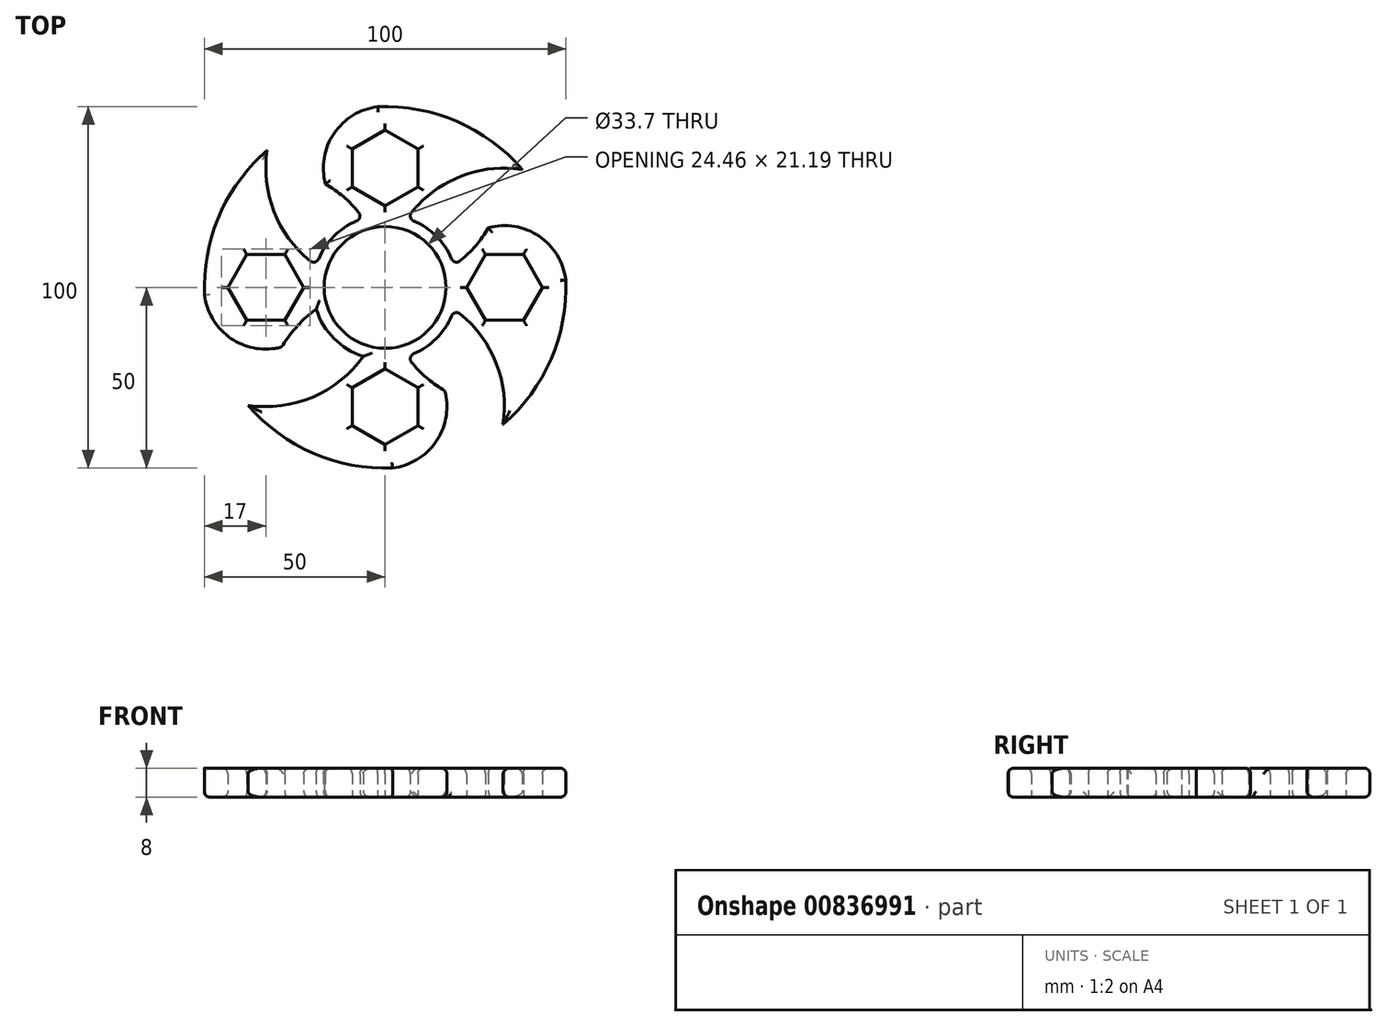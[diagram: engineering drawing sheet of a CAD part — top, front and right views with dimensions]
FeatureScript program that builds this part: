
annotation { "Feature Type Name" : "Feature", "Feature Type Description" : "" }
export const myFeature = defineFeature(function(context is Context, id is Id, definition is map)
    precondition{}
    {
        {
            var Q0;
            Q0=qCreatedBy(makeId("Top.planeOp"),FACE);
            var sketch = newSketch(context, id + "F0", { "sketchPlane" : qUnion([Q0])});
            skCircle(sketch, "E0", {"center": v(0, 0) * mm, "radius": 16.85 * mm});
            skArc(sketch, "E1", {"start": v(-19.06, -6.06) * mm, "mid": v(-14.14, -14.14) * mm, "end": v(-6.06, -19.06) * mm});
            skLineSegment(sketch, "E2.0", {"start": v(-22.5, 0) * mm, "end": v(-27.75, -9.1) * mm});
            skLineSegment(sketch, "E2.1", {"start": v(-27.75, -9.1) * mm, "end": v(-38.25, -9.1) * mm});
            skLineSegment(sketch, "E2.2", {"start": v(-38.25, -9.1) * mm, "end": v(-43.5, 0) * mm});
            skLineSegment(sketch, "E2.3", {"start": v(-43.5, 0) * mm, "end": v(-38.25, 9.1) * mm});
            skLineSegment(sketch, "E2.4", {"start": v(-38.25, 9.1) * mm, "end": v(-27.75, 9.1) * mm});
            skLineSegment(sketch, "E2.5", {"start": v(-27.75, 9.1) * mm, "end": v(-22.5, 0) * mm});
            skLineSegment(sketch, "E3.0", {"start": v(0, 22.5) * mm, "end": v(-9.1, 27.75) * mm});
            skLineSegment(sketch, "E3.1", {"start": v(-9.1, 27.75) * mm, "end": v(-9.1, 38.25) * mm});
            skLineSegment(sketch, "E3.2", {"start": v(-9.1, 38.25) * mm, "end": v(0, 43.5) * mm});
            skLineSegment(sketch, "E3.3", {"start": v(0, 43.5) * mm, "end": v(9.1, 38.25) * mm});
            skLineSegment(sketch, "E3.4", {"start": v(9.1, 38.25) * mm, "end": v(9.1, 27.75) * mm});
            skLineSegment(sketch, "E3.5", {"start": v(9.1, 27.75) * mm, "end": v(0, 22.5) * mm});
            skLineSegment(sketch, "E4.0", {"start": v(22.5, 0) * mm, "end": v(27.75, 9.1) * mm});
            skLineSegment(sketch, "E4.1", {"start": v(27.75, 9.1) * mm, "end": v(38.25, 9.1) * mm});
            skLineSegment(sketch, "E4.2", {"start": v(38.25, 9.1) * mm, "end": v(43.5, 0) * mm});
            skLineSegment(sketch, "E4.3", {"start": v(43.5, 0) * mm, "end": v(38.25, -9.1) * mm});
            skLineSegment(sketch, "E4.4", {"start": v(38.25, -9.1) * mm, "end": v(27.75, -9.1) * mm});
            skLineSegment(sketch, "E4.5", {"start": v(27.75, -9.1) * mm, "end": v(22.5, 0) * mm});
            skLineSegment(sketch, "E5.0", {"start": v(0, -22.5) * mm, "end": v(9.1, -27.75) * mm});
            skLineSegment(sketch, "E5.1", {"start": v(9.1, -27.75) * mm, "end": v(9.1, -38.25) * mm});
            skLineSegment(sketch, "E5.2", {"start": v(9.1, -38.25) * mm, "end": v(0, -43.5) * mm});
            skLineSegment(sketch, "E5.3", {"start": v(0, -43.5) * mm, "end": v(-9.1, -38.25) * mm});
            skLineSegment(sketch, "E5.4", {"start": v(-9.1, -38.25) * mm, "end": v(-9.1, -27.75) * mm});
            skLineSegment(sketch, "E5.5", {"start": v(-9.1, -27.75) * mm, "end": v(0, -22.5) * mm});
            skArc(sketch, "E6", {"start": v(32.64, -37.88) * mm, "mid": v(30.35, -20.05) * mm, "end": v(19.06, -6.06) * mm});
            skArc(sketch, "E7", {"start": v(37.88, 32.64) * mm, "mid": v(20.05, 30.35) * mm, "end": v(6.06, 19.06) * mm});
            skArc(sketch, "E8", {"start": v(-32.64, 37.88) * mm, "mid": v(-45.87, 19.9) * mm, "end": v(-49.96, -2.06) * mm});
            skPoint(sketch, "E9", {"position": v(-28.58, -16.5) * mm});
            skArc(sketch, "E10.trimOffspring", {"start": v(-49.96, -2.06) * mm, "mid": v(-42.56, -14.15) * mm, "end": v(-28.58, -16.5) * mm});
            skArc(sketch, "E11.trimOffspring", {"start": v(-37.88, -32.64) * mm, "mid": v(-20.05, -30.35) * mm, "end": v(-6.06, -19.06) * mm});
            skArc(sketch, "E12.trimOffspring", {"start": v(0, -0.7) * mm, "mid": v(0, -0.7) * mm, "end": v(0, -0.7) * mm});
            skArc(sketch, "E13.trimOffspring", {"start": v(-32.64, 37.88) * mm, "mid": v(-30.35, 20.05) * mm, "end": v(-19.06, 6.06) * mm});
            skArc(sketch, "E14.trimOffspring", {"start": v(-6.06, 19.06) * mm, "mid": v(-10.76, 24.38) * mm, "end": v(-16.5, 28.58) * mm});
            skArc(sketch, "E15.trimOffspring", {"start": v(-6.06, 19.06) * mm, "mid": v(-14.14, 14.14) * mm, "end": v(-19.06, 6.06) * mm});
            skArc(sketch, "E16.trimOffspring", {"start": v(-2.06, 49.96) * mm, "mid": v(-14.15, 42.56) * mm, "end": v(-16.5, 28.58) * mm});
            skArc(sketch, "E17.trimOffspring", {"start": v(37.88, 32.64) * mm, "mid": v(19.9, 45.87) * mm, "end": v(-2.06, 49.96) * mm});
            skArc(sketch, "E18.trimOffspring", {"start": v(49.96, 2.06) * mm, "mid": v(42.56, 14.15) * mm, "end": v(28.58, 16.5) * mm});
            skArc(sketch, "E19.trimOffspring", {"start": v(-37.88, -32.64) * mm, "mid": v(-19.9, -45.87) * mm, "end": v(2.06, -49.96) * mm});
            skArc(sketch, "E20.trimOffspring", {"start": v(32.64, -37.88) * mm, "mid": v(45.87, -19.9) * mm, "end": v(49.96, 2.06) * mm});
            skArc(sketch, "E21.trimOffspring", {"start": v(2.06, -49.96) * mm, "mid": v(14.15, -42.56) * mm, "end": v(16.5, -28.58) * mm});
            skArc(sketch, "E22.trimOffspring", {"start": v(-19.06, -6.06) * mm, "mid": v(-24.38, -10.76) * mm, "end": v(-28.58, -16.5) * mm});
            skArc(sketch, "E23.trimOffspring", {"start": v(0, 0.7) * mm, "mid": v(0, 0.7) * mm, "end": v(0, 0.7) * mm});
            skArc(sketch, "E24.trimOffspring", {"start": v(6.06, -19.06) * mm, "mid": v(10.76, -24.38) * mm, "end": v(16.5, -28.58) * mm});
            skArc(sketch, "E25.trimOffspring", {"start": v(6.06, -19.06) * mm, "mid": v(14.14, -14.14) * mm, "end": v(19.06, -6.06) * mm});
            skArc(sketch, "E26.trimOffspring", {"start": v(19.06, 6.06) * mm, "mid": v(14.14, 14.14) * mm, "end": v(6.06, 19.06) * mm});
            skArc(sketch, "E27.trimOffspring", {"start": v(19.06, 6.06) * mm, "mid": v(24.38, 10.76) * mm, "end": v(28.58, 16.5) * mm});
            skSolve(sketch);
        }
        {
            var Q0;
            Q0 = qSketchRegion(id + "F0", true);
            extrude(context, id + "F1", {"entities" : qUnion([Q0]), "depth" : 8 * mm, "offsetDistance" : 25 * mm});
        }
        {
            var Q0;
            Q0=makeQuery(id+"F1.opExtrude","CAP_EDGE",EDGE,{"disambiguationData":[OSD([sQuery(id+"F0.wireOp",EDGE,"E5.3")])],"isStart":false});
            var Q1;
            Q1=makeQuery(id+"F1.opExtrude","CAP_EDGE",EDGE,{"disambiguationData":[OSD([sQuery(id+"F0.wireOp",EDGE,"E5.2")])],"isStart":false});
            var Q2;
            Q2=makeQuery(id+"F1.opExtrude","CAP_EDGE",EDGE,{"disambiguationData":[OSD([sQuery(id+"F0.wireOp",EDGE,"E5.4")])],"isStart":false});
            var Q3;
            Q3=makeQuery(id+"F1.opExtrude","CAP_EDGE",EDGE,{"disambiguationData":[OSD([sQuery(id+"F0.wireOp",EDGE,"E5.5")])],"isStart":false});
            var Q4;
            Q4=makeQuery(id+"F1.opExtrude","CAP_EDGE",EDGE,{"disambiguationData":[OSD([sQuery(id+"F0.wireOp",EDGE,"E5.0")])],"isStart":false});
            var Q5;
            Q5=makeQuery(id+"F1.opExtrude","CAP_EDGE",EDGE,{"disambiguationData":[OSD([sQuery(id+"F0.wireOp",EDGE,"E5.1")])],"isStart":false});
            var Q6;
            Q6=makeQuery(id+"F1.opExtrude","CAP_EDGE",EDGE,{"disambiguationData":[OSD([sQuery(id+"F0.wireOp",EDGE,"E24.trimOffspring")])],"isStart":false});
            var Q7;
            Q7=makeQuery(id+"F1.opExtrude","CAP_EDGE",EDGE,{"disambiguationData":[OSD([sQuery(id+"F0.wireOp",EDGE,"E21.trimOffspring")])],"isStart":false});
            var Q8;
            Q8=makeQuery(id+"F1.opExtrude","SWEPT_EDGE",EDGE,{"disambiguationData":[OSD([sQuery(id+"F0.wireOp",EDGE,"E21.trimOffspring"),sQuery(id+"F0.wireOp",EDGE,"E24.trimOffspring")])]});
            var Q9;
            Q9=makeQuery(id+"F1.opExtrude","CAP_EDGE",EDGE,{"disambiguationData":[OSD([sQuery(id+"F0.wireOp",EDGE,"E11.trimOffspring")])],"isStart":false});
            var Q10;
            Q10=makeQuery(id+"F1.opExtrude","CAP_EDGE",EDGE,{"disambiguationData":[OSD([sQuery(id+"F0.wireOp",EDGE,"E25.trimOffspring")])],"isStart":false});
            var Q11;
            Q11=makeQuery(id+"F1.opExtrude","SWEPT_EDGE",EDGE,{"disambiguationData":[OSD([sQuery(id+"F0.wireOp",EDGE,"E24.trimOffspring"),sQuery(id+"F0.wireOp",EDGE,"E25.trimOffspring")])]});
            var Q12;
            Q12=makeQuery(id+"F1.opExtrude","CAP_EDGE",EDGE,{"disambiguationData":[OSD([sQuery(id+"F0.wireOp",EDGE,"E6")])],"isStart":false});
            var Q13;
            Q13=makeQuery(id+"F1.opExtrude","CAP_EDGE",EDGE,{"disambiguationData":[OSD([sQuery(id+"F0.wireOp",EDGE,"E27.trimOffspring")])],"isStart":false});
            var Q14;
            Q14=makeQuery(id+"F1.opExtrude","SWEPT_EDGE",EDGE,{"disambiguationData":[OSD([sQuery(id+"F0.wireOp",EDGE,"E7"),sQuery(id+"F0.wireOp",EDGE,"E26.trimOffspring")])]});
            var Q15;
            Q15=makeQuery(id+"F1.opExtrude","CAP_EDGE",EDGE,{"disambiguationData":[OSD([sQuery(id+"F0.wireOp",EDGE,"E26.trimOffspring")])],"isStart":false});
            var Q16;
            Q16=makeQuery(id+"F1.opExtrude","CAP_EDGE",EDGE,{"disambiguationData":[OSD([sQuery(id+"F0.wireOp",EDGE,"E17.trimOffspring")])],"isStart":false});
            var Q17;
            Q17=makeQuery(id+"F1.opExtrude","CAP_EDGE",EDGE,{"disambiguationData":[OSD([sQuery(id+"F0.wireOp",EDGE,"E14.trimOffspring")])],"isStart":false});
            var Q18;
            Q18=makeQuery(id+"F1.opExtrude","CAP_EDGE",EDGE,{"disambiguationData":[OSD([sQuery(id+"F0.wireOp",EDGE,"E16.trimOffspring")])],"isStart":false});
            var Q19;
            Q19=makeQuery(id+"F1.opExtrude","CAP_EDGE",EDGE,{"disambiguationData":[OSD([sQuery(id+"F0.wireOp",EDGE,"E13.trimOffspring")])],"isStart":false});
            var Q20;
            Q20=makeQuery(id+"F1.opExtrude","CAP_EDGE",EDGE,{"disambiguationData":[OSD([sQuery(id+"F0.wireOp",EDGE,"E13.trimOffspring")])],"isStart":true});
            var Q21;
            Q21=makeQuery(id+"F1.opExtrude","SWEPT_EDGE",EDGE,{"disambiguationData":[OSD([sQuery(id+"F0.wireOp",EDGE,"E10.trimOffspring"),sQuery(id+"F0.wireOp",EDGE,"E22.trimOffspring")])]});
            var Q22;
            Q22=makeQuery(id+"F1.opExtrude","CAP_EDGE",EDGE,{"disambiguationData":[OSD([sQuery(id+"F0.wireOp",EDGE,"E22.trimOffspring")])],"isStart":true});
            var Q23;
            Q23=makeQuery(id+"F1.opExtrude","CAP_EDGE",EDGE,{"disambiguationData":[OSD([sQuery(id+"F0.wireOp",EDGE,"E22.trimOffspring")])],"isStart":false});
            var Q24;
            Q24=makeQuery(id+"F1.opExtrude","CAP_EDGE",EDGE,{"disambiguationData":[OSD([sQuery(id+"F0.wireOp",EDGE,"E15.trimOffspring")])],"isStart":false});
            var Q25;
            Q25=makeQuery(id+"F1.opExtrude","CAP_EDGE",EDGE,{"disambiguationData":[OSD([sQuery(id+"F0.wireOp",EDGE,"E1")])],"isStart":false});
            var Q26;
            Q26=makeQuery(id+"F1.opExtrude","CAP_EDGE",EDGE,{"disambiguationData":[OSD([sQuery(id+"F0.wireOp",EDGE,"E2.0")])],"isStart":false});
            var Q27;
            Q27=makeQuery(id+"F1.opExtrude","CAP_EDGE",EDGE,{"disambiguationData":[OSD([sQuery(id+"F0.wireOp",EDGE,"E2.1")])],"isStart":false});
            var Q28;
            Q28=makeQuery(id+"F1.opExtrude","CAP_EDGE",EDGE,{"disambiguationData":[OSD([sQuery(id+"F0.wireOp",EDGE,"E2.2")])],"isStart":false});
            var Q29;
            Q29=makeQuery(id+"F1.opExtrude","CAP_EDGE",EDGE,{"disambiguationData":[OSD([sQuery(id+"F0.wireOp",EDGE,"E2.3")])],"isStart":false});
            var Q30;
            Q30=makeQuery(id+"F1.opExtrude","CAP_EDGE",EDGE,{"disambiguationData":[OSD([sQuery(id+"F0.wireOp",EDGE,"E2.4")])],"isStart":false});
            var Q31;
            Q31=makeQuery(id+"F1.opExtrude","CAP_EDGE",EDGE,{"disambiguationData":[OSD([sQuery(id+"F0.wireOp",EDGE,"E2.5")])],"isStart":false});
            var Q32;
            Q32=makeQuery(id+"F1.opExtrude","CAP_EDGE",EDGE,{"disambiguationData":[OSD([sQuery(id+"F0.wireOp",EDGE,"E20.trimOffspring")])],"isStart":false});
            var Q33;
            Q33=makeQuery(id+"F1.opExtrude","CAP_EDGE",EDGE,{"disambiguationData":[OSD([sQuery(id+"F0.wireOp",EDGE,"E18.trimOffspring")])],"isStart":false});
            var Q34;
            Q34=makeQuery(id+"F1.opExtrude","CAP_EDGE",EDGE,{"disambiguationData":[OSD([sQuery(id+"F0.wireOp",EDGE,"E4.4")])],"isStart":false});
            var Q35;
            Q35=makeQuery(id+"F1.opExtrude","CAP_EDGE",EDGE,{"disambiguationData":[OSD([sQuery(id+"F0.wireOp",EDGE,"E4.5")])],"isStart":false});
            var Q36;
            Q36=makeQuery(id+"F1.opExtrude","CAP_EDGE",EDGE,{"disambiguationData":[OSD([sQuery(id+"F0.wireOp",EDGE,"E4.0")])],"isStart":false});
            var Q37;
            Q37=makeQuery(id+"F1.opExtrude","CAP_EDGE",EDGE,{"disambiguationData":[OSD([sQuery(id+"F0.wireOp",EDGE,"E4.1")])],"isStart":false});
            var Q38;
            Q38=makeQuery(id+"F1.opExtrude","CAP_EDGE",EDGE,{"disambiguationData":[OSD([sQuery(id+"F0.wireOp",EDGE,"E4.2")])],"isStart":false});
            var Q39;
            Q39=makeQuery(id+"F1.opExtrude","CAP_EDGE",EDGE,{"disambiguationData":[OSD([sQuery(id+"F0.wireOp",EDGE,"E4.3")])],"isStart":false});
            var Q40;
            Q40=makeQuery(id+"F1.opExtrude","CAP_EDGE",EDGE,{"disambiguationData":[OSD([sQuery(id+"F0.wireOp",EDGE,"E3.2")])],"isStart":false});
            var Q41;
            Q41=makeQuery(id+"F1.opExtrude","CAP_EDGE",EDGE,{"disambiguationData":[OSD([sQuery(id+"F0.wireOp",EDGE,"E3.1")])],"isStart":false});
            var Q42;
            Q42=makeQuery(id+"F1.opExtrude","CAP_EDGE",EDGE,{"disambiguationData":[OSD([sQuery(id+"F0.wireOp",EDGE,"E3.0")])],"isStart":false});
            var Q43;
            Q43=makeQuery(id+"F1.opExtrude","CAP_EDGE",EDGE,{"disambiguationData":[OSD([sQuery(id+"F0.wireOp",EDGE,"E3.5")])],"isStart":false});
            var Q44;
            Q44=makeQuery(id+"F1.opExtrude","CAP_EDGE",EDGE,{"disambiguationData":[OSD([sQuery(id+"F0.wireOp",EDGE,"E3.4")])],"isStart":false});
            var Q45;
            Q45=makeQuery(id+"F1.opExtrude","CAP_EDGE",EDGE,{"disambiguationData":[OSD([sQuery(id+"F0.wireOp",EDGE,"E3.3")])],"isStart":false});
            var Q46;
            Q46=makeQuery(id+"F1.opExtrude","CAP_EDGE",EDGE,{"disambiguationData":[OSD([sQuery(id+"F0.wireOp",EDGE,"E14.trimOffspring")])],"isStart":true});
            var Q47;
            Q47=makeQuery(id+"F1.opExtrude","CAP_EDGE",EDGE,{"disambiguationData":[OSD([sQuery(id+"F0.wireOp",EDGE,"E15.trimOffspring")])],"isStart":true});
            var Q48;
            Q48=makeQuery(id+"F1.opExtrude","CAP_EDGE",EDGE,{"disambiguationData":[OSD([sQuery(id+"F0.wireOp",EDGE,"E7")])],"isStart":true});
            var Q49;
            Q49=makeQuery(id+"F1.opExtrude","CAP_EDGE",EDGE,{"disambiguationData":[OSD([sQuery(id+"F0.wireOp",EDGE,"E17.trimOffspring")])],"isStart":true});
            var Q50;
            Q50=makeQuery(id+"F1.opExtrude","CAP_EDGE",EDGE,{"disambiguationData":[OSD([sQuery(id+"F0.wireOp",EDGE,"E16.trimOffspring")])],"isStart":true});
            var Q51;
            Q51=makeQuery(id+"F1.opExtrude","CAP_EDGE",EDGE,{"disambiguationData":[OSD([sQuery(id+"F0.wireOp",EDGE,"E8")])],"isStart":true});
            var Q52;
            Q52=makeQuery(id+"F1.opExtrude","CAP_EDGE",EDGE,{"disambiguationData":[OSD([sQuery(id+"F0.wireOp",EDGE,"E10.trimOffspring")])],"isStart":true});
            var Q53;
            Q53=makeQuery(id+"F1.opExtrude","CAP_EDGE",EDGE,{"disambiguationData":[OSD([sQuery(id+"F0.wireOp",EDGE,"E2.3")])],"isStart":true});
            var Q54;
            Q54=makeQuery(id+"F1.opExtrude","CAP_EDGE",EDGE,{"disambiguationData":[OSD([sQuery(id+"F0.wireOp",EDGE,"E2.4")])],"isStart":true});
            var Q55;
            Q55=makeQuery(id+"F1.opExtrude","CAP_EDGE",EDGE,{"disambiguationData":[OSD([sQuery(id+"F0.wireOp",EDGE,"E2.5")])],"isStart":true});
            var Q56;
            Q56=makeQuery(id+"F1.opExtrude","CAP_EDGE",EDGE,{"disambiguationData":[OSD([sQuery(id+"F0.wireOp",EDGE,"E2.0")])],"isStart":true});
            var Q57;
            Q57=makeQuery(id+"F1.opExtrude","CAP_EDGE",EDGE,{"disambiguationData":[OSD([sQuery(id+"F0.wireOp",EDGE,"E2.1")])],"isStart":true});
            var Q58;
            Q58=makeQuery(id+"F1.opExtrude","CAP_EDGE",EDGE,{"disambiguationData":[OSD([sQuery(id+"F0.wireOp",EDGE,"E2.2")])],"isStart":true});
            var Q59;
            Q59=makeQuery(id+"F1.opExtrude","CAP_EDGE",EDGE,{"disambiguationData":[OSD([sQuery(id+"F0.wireOp",EDGE,"E1")])],"isStart":true});
            var Q60;
            Q60=makeQuery(id+"F1.opExtrude","CAP_EDGE",EDGE,{"disambiguationData":[OSD([sQuery(id+"F0.wireOp",EDGE,"E25.trimOffspring")])],"isStart":true});
            var Q61;
            Q61=makeQuery(id+"F1.opExtrude","CAP_EDGE",EDGE,{"disambiguationData":[OSD([sQuery(id+"F0.wireOp",EDGE,"E6")])],"isStart":true});
            var Q62;
            Q62=makeQuery(id+"F1.opExtrude","CAP_EDGE",EDGE,{"disambiguationData":[OSD([sQuery(id+"F0.wireOp",EDGE,"E27.trimOffspring")])],"isStart":true});
            var Q63;
            Q63=makeQuery(id+"F1.opExtrude","CAP_EDGE",EDGE,{"disambiguationData":[OSD([sQuery(id+"F0.wireOp",EDGE,"E18.trimOffspring")])],"isStart":true});
            var Q64;
            Q64=makeQuery(id+"F1.opExtrude","CAP_EDGE",EDGE,{"disambiguationData":[OSD([sQuery(id+"F0.wireOp",EDGE,"E19.trimOffspring")])],"isStart":true});
            var Q65;
            Q65=makeQuery(id+"F1.opExtrude","CAP_EDGE",EDGE,{"disambiguationData":[OSD([sQuery(id+"F0.wireOp",EDGE,"E21.trimOffspring")])],"isStart":true});
            var Q66;
            Q66=makeQuery(id+"F1.opExtrude","CAP_EDGE",EDGE,{"disambiguationData":[OSD([sQuery(id+"F0.wireOp",EDGE,"E11.trimOffspring")])],"isStart":true});
            var Q67;
            Q67=makeQuery(id+"F1.opExtrude","SWEPT_EDGE",EDGE,{"disambiguationData":[OSD([sQuery(id+"F0.wireOp",EDGE,"E6"),sQuery(id+"F0.wireOp",EDGE,"E25.trimOffspring")])]});
            var Q68;
            Q68=makeQuery(id+"F1.opExtrude","SWEPT_EDGE",EDGE,{"disambiguationData":[OSD([sQuery(id+"F0.wireOp",EDGE,"E13.trimOffspring"),sQuery(id+"F0.wireOp",EDGE,"E15.trimOffspring")])]});
            var Q69;
            Q69=makeQuery(id+"F1.opExtrude","SWEPT_EDGE",EDGE,{"disambiguationData":[OSD([sQuery(id+"F0.wireOp",EDGE,"E26.trimOffspring"),sQuery(id+"F0.wireOp",EDGE,"E27.trimOffspring")])]});
            var Q70;
            Q70=makeQuery(id+"F1.opExtrude","SWEPT_EDGE",EDGE,{"disambiguationData":[OSD([sQuery(id+"F0.wireOp",EDGE,"E14.trimOffspring"),sQuery(id+"F0.wireOp",EDGE,"E15.trimOffspring")])]});
            fillet(context, id + "F2", {"entities" : qUnion([Q0, Q1, Q2, Q3, Q4, Q5, Q6, Q7, Q8, Q9, Q10, Q11, Q12, Q13, Q14, Q15, Q16, Q17, Q18, Q19, Q20, Q21, Q22, Q23, Q24, Q25, Q26, Q27, Q28, Q29, Q30, Q31, Q32, Q33, Q34, Q35, Q36, Q37, Q38, Q39, Q40, Q41, Q42, Q43, Q44, Q45, Q46, Q47, Q48, Q49, Q50, Q51, Q52, Q53, Q54, Q55, Q56, Q57, Q58, Q59, Q60, Q61, Q62, Q63, Q64, Q65, Q66, Q67, Q68, Q69, Q70]), "radius" : 1.5 * mm, "tangentPropagation" : true, "allowEdgeOverflow" : false});
        }
    });
